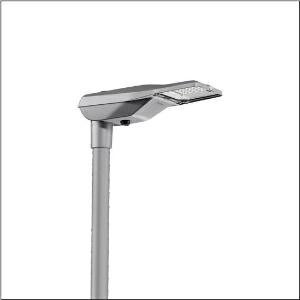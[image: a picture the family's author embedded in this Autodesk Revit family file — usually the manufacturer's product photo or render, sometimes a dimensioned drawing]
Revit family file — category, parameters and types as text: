
# Revit family: streetlight_sl_21_micro___st1_0a_5xe1d33r08db_e2a0
name_source: partatom
category: Lighting Fixtures
units: mm (PartAtom-declared; Revit-internal decimal feet)

## family parameters
Cut with Voids When Loaded = No
Host = Face
Light Source = No
Part Type = Normal
Room Calculation Point = No
Round Connector Dimension = Use Diameter
Shared = No

## types (1)
- --- (1 x LED, 5110 lm, 39.1 W, 3000K)
    Apparent Load = 39 VA
    CIE Flux Codes = 37 72 97 100 100
    Color Rendering = 70
    Color Temperature = 3000K
    Default Elevation = 1800 mm
    Description = Streetlight SL 21 micro, mast luminaire, primary light control with lens, of PMMA, primary optical cover: cover, of toughened safety glass, transparent, light distribution: ST1.0a, light emission: direct distribution, primary light characteristic: asymmetric, installation type: side-entry, post-top, LED, High Power LED, rated luminous flux: 5.110lm, luminous efficacy: 131lm/W, light colour: 730, colour temperature: 3000K, control gear: D4i, control: flexible luminous flux parameterisation, time-dependent luminous flux control, constant luminous flux control, overheat protection, pre-setting: logarithmic dimming characteristic, mains connection: 220..240V, AC, 50/60Hz, start of lifetime: 39W, end of service life: 41W, reduction: 18W, luminaire housing, of diecast aluminium, powder-coated, Siteco® metallic grey (DB 702S), corrosivity category C5 mid according to DIN EN ISO 12944, please order mast flange separately, inclination adjustable: 0°, 5°, 10°, 15°, sealing non-destructively replaceable, multi-level sealing system, length: 528mm, width: 235mm, height: 110mm, mast flange for spigot size: 42mm (side-entry): 5XC10008XM4, 60/48mm (side-entry/post-top): 5XC10108XM2, 76/60mm (side-entry/post-top): 5XC10108XM1, Smart Interface below, protection rating (complete): IP66, insulation class (complete): insulation class II (safety insulation), certification: CE, ENEC, ENEC+, VDE, impact resistance: IK09, permissible operating ambient temperature for outdoor applications: -40..+50°C, standard-compliant lighting for roads and squares, packaging unit: 1 piece

Light Distribution: ST1.0a
    Height = 110 mm
    Lamp = 1 x LED
    Lamp Light Flux = 5110 lm
    Lamp Power = 39.1 W
    Lamp count = 1
    Length = 528 mm
    Luminous efficacy = 131 lm/W
    Manufacturer = Siteco
    ModVariant = No
    Model = 5XE1D33R08DB
    Number of Poles = 1
    OnlyDefault = Yes
    Power Factor = 1
    Product Name = Streetlight SL 21 micro | ST1.0a
    Product group = mast luminaire | pylon top
    ProductGroupID = 6100
    Protection Class = Protection class II
    Protection Degree = IP 66
    RLX_Detail_Level = 1
    RLX_Emergency_Light_Flux = 0 lm
    RLX_Emergency_Type = 0
    RLX_Emergency_Type_DB = No
    RlxData = <blob elided: 99605 chars, md5=24df7fc6>
    Socket = socket
    Standby Power = 0 W
    System Light Flux = 5110 lm
    System Power = 39 W
    Type Comments = factory setting: luminous flux: 100 % | dim-lin: 254 | 765 mA
    Type Image = l_1277290.jpg
    URL = http://relux.com
    VarID = @adj_151542
    Voltage = 0 V
    Weight = 0.00 kg
    Width = 235 mm

## geometry (parser evidence)
native form markers: Blend x4, Sweep x10
no freeform markers — native parametric forms only
